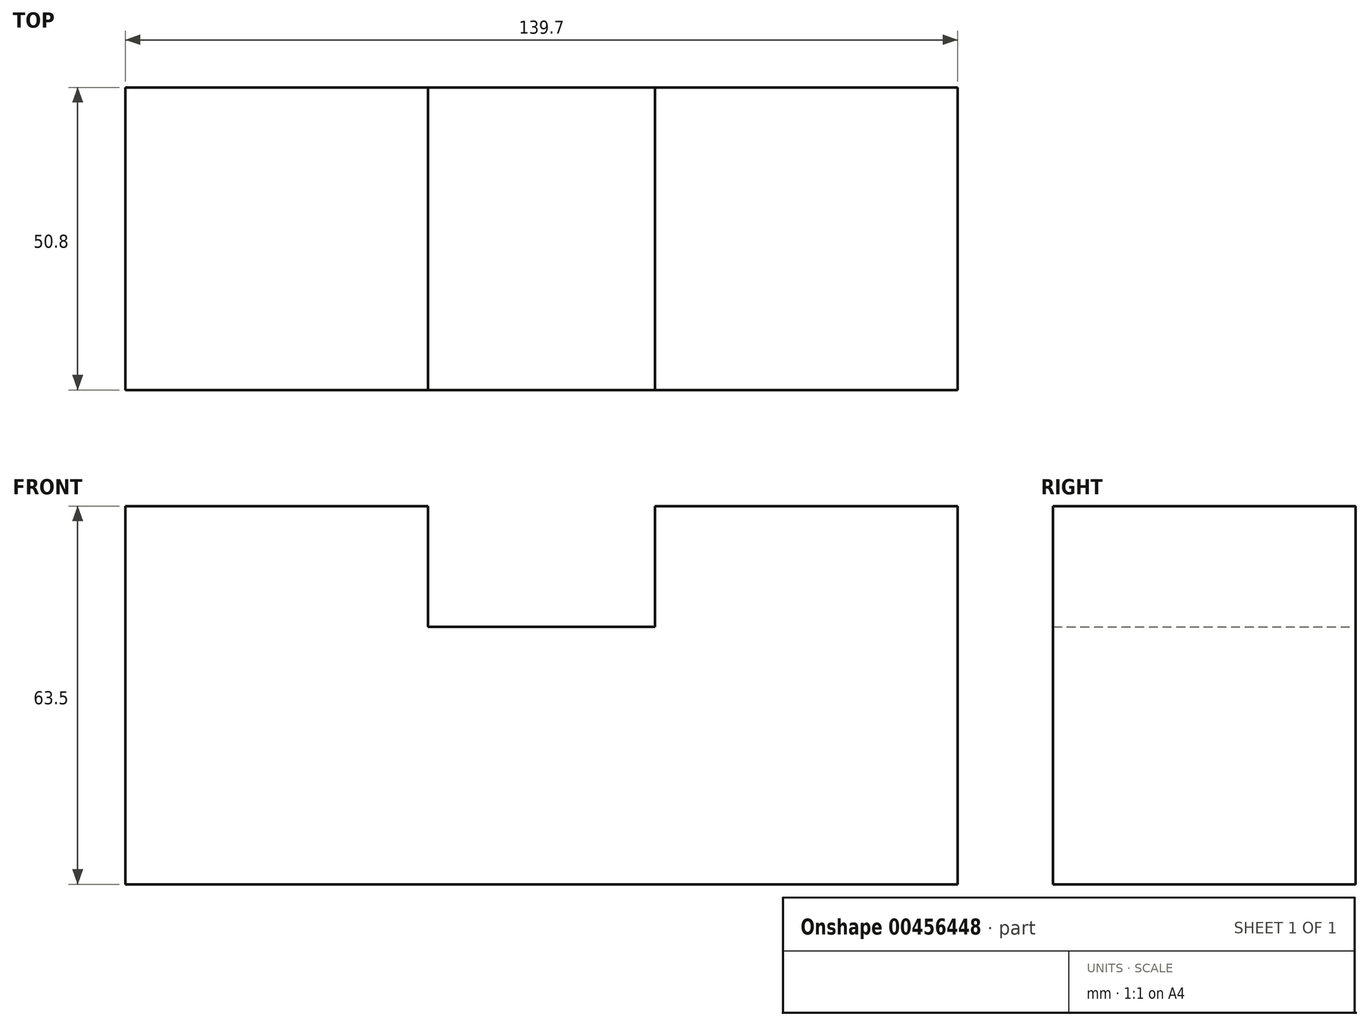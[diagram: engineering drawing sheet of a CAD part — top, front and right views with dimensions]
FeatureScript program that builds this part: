
annotation { "Feature Type Name" : "Feature", "Feature Type Description" : "" }
export const myFeature = defineFeature(function(context is Context, id is Id, definition is map)
    precondition{}
    {
        {
            var Q0;
            Q0=qCreatedBy(makeId("Front.planeOp"),FACE);
            var sketch = newSketch(context, id + "F0", { "sketchPlane" : qUnion([Q0])});
            skLineSegment(sketch, "E0.bottom", {"start": v(-71.2, -55.16) * mm, "end": v(68.5, -55.16) * mm});
            skLineSegment(sketch, "E0.top", {"start": v(-71.2, 8.34) * mm, "end": v(-20.4, 8.34) * mm});
            skLineSegment(sketch, "E0.left", {"start": v(-71.2, -55.16) * mm, "end": v(-71.2, 8.34) * mm});
            skLineSegment(sketch, "E0.right", {"start": v(68.5, -55.16) * mm, "end": v(68.5, 8.34) * mm});
            skLineSegment(sketch, "E1.bottom", {"start": v(-20.4, -11.96) * mm, "end": v(17.7, -11.96) * mm});
            skLineSegment(sketch, "E1.left", {"start": v(-20.4, -11.96) * mm, "end": v(-20.4, 8.34) * mm});
            skLineSegment(sketch, "E1.right", {"start": v(17.7, -11.96) * mm, "end": v(17.7, 8.34) * mm});
            skLineSegment(sketch, "E2.trimOffspring", {"start": v(17.7, 8.34) * mm, "end": v(68.5, 8.34) * mm});
            skSolve(sketch);
        }
        {
            var Q0;
            Q0 = qSketchRegion(id + "F0", true);
            extrude(context, id + "F1", {"entities" : qUnion([Q0]), "depth" : 50.8 * mm});
        }
    });
